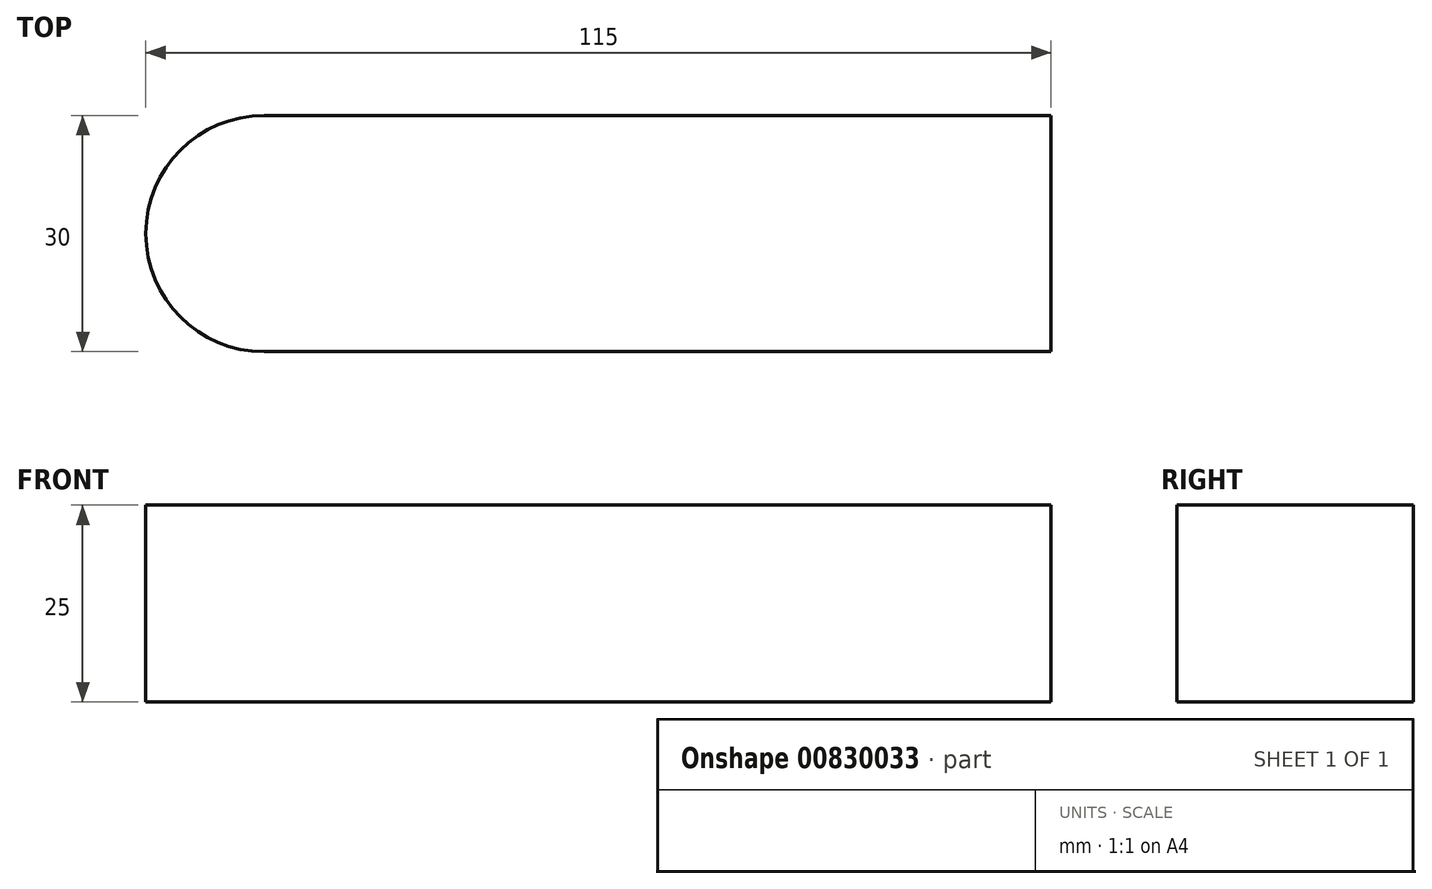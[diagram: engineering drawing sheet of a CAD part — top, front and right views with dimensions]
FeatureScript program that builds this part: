
annotation { "Feature Type Name" : "Feature", "Feature Type Description" : "" }
export const myFeature = defineFeature(function(context is Context, id is Id, definition is map)
    precondition{}
    {
        {
            var Q0;
            Q0=qCreatedBy(makeId("Top.planeOp"),FACE);
            var sketch = newSketch(context, id + "F0", { "sketchPlane" : qUnion([Q0])});
            skLineSegment(sketch, "E0.bottom", {"start": v(-48.64, 3.28) * mm, "end": v(51.36, 3.28) * mm});
            skLineSegment(sketch, "E0.top", {"start": v(-48.64, -26.72) * mm, "end": v(51.36, -26.72) * mm});
            skLineSegment(sketch, "E0.left", {"start": v(-48.64, 3.28) * mm, "end": v(-48.64, -26.72) * mm});
            skLineSegment(sketch, "E0.right", {"start": v(51.36, 3.28) * mm, "end": v(51.36, -26.72) * mm});
            skCircle(sketch, "E1", {"center": v(-48.64, -11.72) * mm, "radius": 15 * mm});
            skSolve(sketch);
        }
        {
            var Q0;
            {var subQ0=sQuery(id+"F0.wireOp",EDGE,"E0.left");Q0=makeQuery(id+"F0.imprint","IMPRINT",FACE,{"disambiguationData":[TD([[makeQuery(id+"F0.imprint","IMPRINT",EDGE,{"derivedFrom":subQ0}),1.0]])]});}
            var Q1;
            {var subQ0=sQuery(id+"F0.wireOp",EDGE,"E0.bottom");Q1=makeQuery(id+"F0.imprint","IMPRINT",FACE,{"disambiguationData":[TD([[makeQuery(id+"F0.imprint","IMPRINT",EDGE,{"derivedFrom":subQ0}),-1.0]])]});}
            var Q2;
            {var subQ0=sQuery(id+"F0.wireOp",EDGE,"E0.left");Q2=makeQuery(id+"F0.imprint","IMPRINT",FACE,{"disambiguationData":[TD([[makeQuery(id+"F0.imprint","IMPRINT",EDGE,{"derivedFrom":subQ0}),-1.0]])]});}
            extrude(context, id + "F1", {"entities" : qUnion([Q0, Q1, Q2]), "depth" : 25 * mm, "offsetDistance" : 25 * mm});
        }
    });
